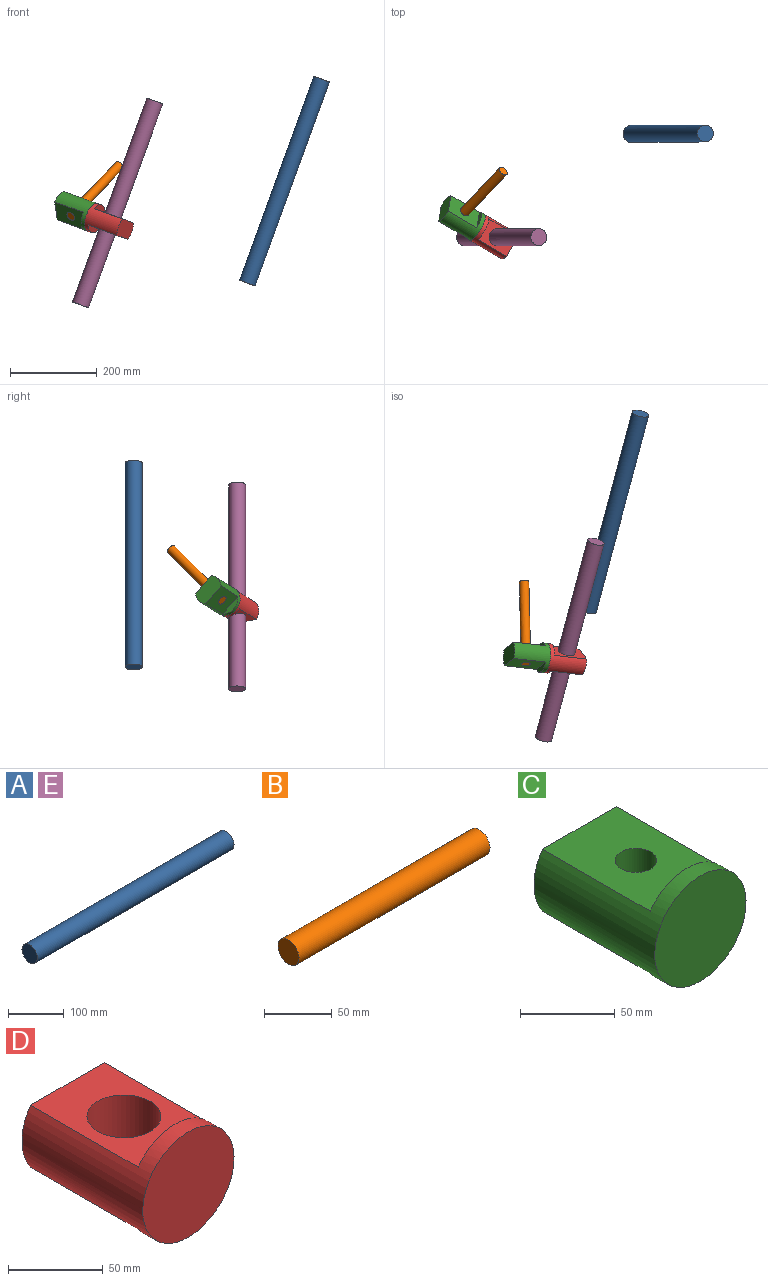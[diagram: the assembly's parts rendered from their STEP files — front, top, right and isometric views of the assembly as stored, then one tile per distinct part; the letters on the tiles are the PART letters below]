
ASSEMBLY  parts=5 mates=4
PART A: 3 faces, bbox 500x39x39 mm
  f0: cylinder r=19.5mm len=500mm, axis (-1,0,0), area 61261.1mm2, adj f1,f2
  f1: plane 39x39mm, normal (1,0,0), area 1194.6mm2, adj f0
  f2: plane 39x39mm, normal (-1,0,0), area 1194.6mm2, adj f0
PART B: 3 faces, bbox 200x22x22 mm
  f0: cylinder r=11mm len=200mm, axis (-1,0,0), area 13823mm2, adj f1,f2
  f1: plane 22x22mm, normal (1,0,0), area 380.1mm2, adj f0
  f2: plane 22x22mm, normal (-1,0,0), area 380.1mm2, adj f0
PART C: 8 faces, bbox 68x90x68 mm
  f0: plane 68.01x40mm, normal (0,1,0), area 2554.1mm2, adj f1,f2,f3
  f1: plane 80x55mm, normal (0,0,1), area 4019.9mm2, adj f0,f3,f4,f7
  f2: plane 80x55mm, normal (0,0,-1), area 4019.9mm2, adj f0,f3,f6,f7
  f3: cylinder r=34mm len=90mm, axis (0,-1,0), area 8978.6mm2, adj f0,f1,f2,f4,f5,f6
  f4: plane 55x14mm, normal (0,1,0), area 539.2mm2, adj f1,f3
  f5: plane 68.01x68.01mm, normal (0,-1,0), area 3632.5mm2, adj f3
  f6: plane 55x14mm, normal (0,1,0), area 539.2mm2, adj f2,f3
  f7: cylinder r=11mm len=40mm, axis (0,0,1), area 2764.6mm2, adj f1,f2
PART D: 8 faces, bbox 68x90x68 mm
  f0: plane 68.01x40mm, normal (0,1,0), area 2554.1mm2, adj f2,f3,f4
  f1: cylinder r=19.5mm len=40mm, axis (0,0,-1), area 4900.9mm2, adj f2,f3
  f2: plane 80x55mm, normal (0,0,1), area 3205.4mm2, adj f0,f1,f4,f5
  f3: plane 80x55mm, normal (0,0,-1), area 3205.4mm2, adj f0,f1,f4,f7
  f4: cylinder r=34mm len=90mm, axis (0,-1,0), area 8978.6mm2, adj f0,f2,f3,f5,f6,f7
  f5: plane 55x14mm, normal (0,1,0), area 539.2mm2, adj f2,f4
  f6: plane 68.01x68.01mm, normal (0,-1,0), area 3632.5mm2, adj f4
  f7: plane 55x14mm, normal (0,1,0), area 539.2mm2, adj f3,f4
PART E: same geometry as A
PLACE A rot(axis=(0,-1,0),70deg) t=(96.95,302.64,-493.85)mm fixed
PLACE B rot(axis=(-0.43,0.85,0.29),156.1deg) t=(-329.85,171.65,-210.39)mm
PLACE C rot(axis=(-0.14,0.66,0.74),85deg) t=(-207.83,-99.34,-361.32)mm
PLACE D rot(axis=(-0.17,0.1,-0.98),119.8deg) t=(-227.61,-87.8,-354.12)mm
PLACE E rot(axis=(0.57,0.14,-0.81),168.9deg) t=(-69.08,-228.05,-91.46)mm
MATE parallel A.f0 <-> E.f0  axis (-0.34,0,-0.94) through (88.27,150.71,-490.69)mm
MATE fastened B.f0 <-> C.f7  axis (-0.56,-0.59,-0.59) through (-317.84,-53.41,-337.07)mm
MATE revolute C.f3 <-> D.f4  axis (0.82,-0.48,-0.3) through (-267.16,-64.72,-339.73)mm
MATE cylindrical D.f1 <-> E.f0  axis (0.34,0,0.94) through (-220.76,-87.8,-335.33)mm
